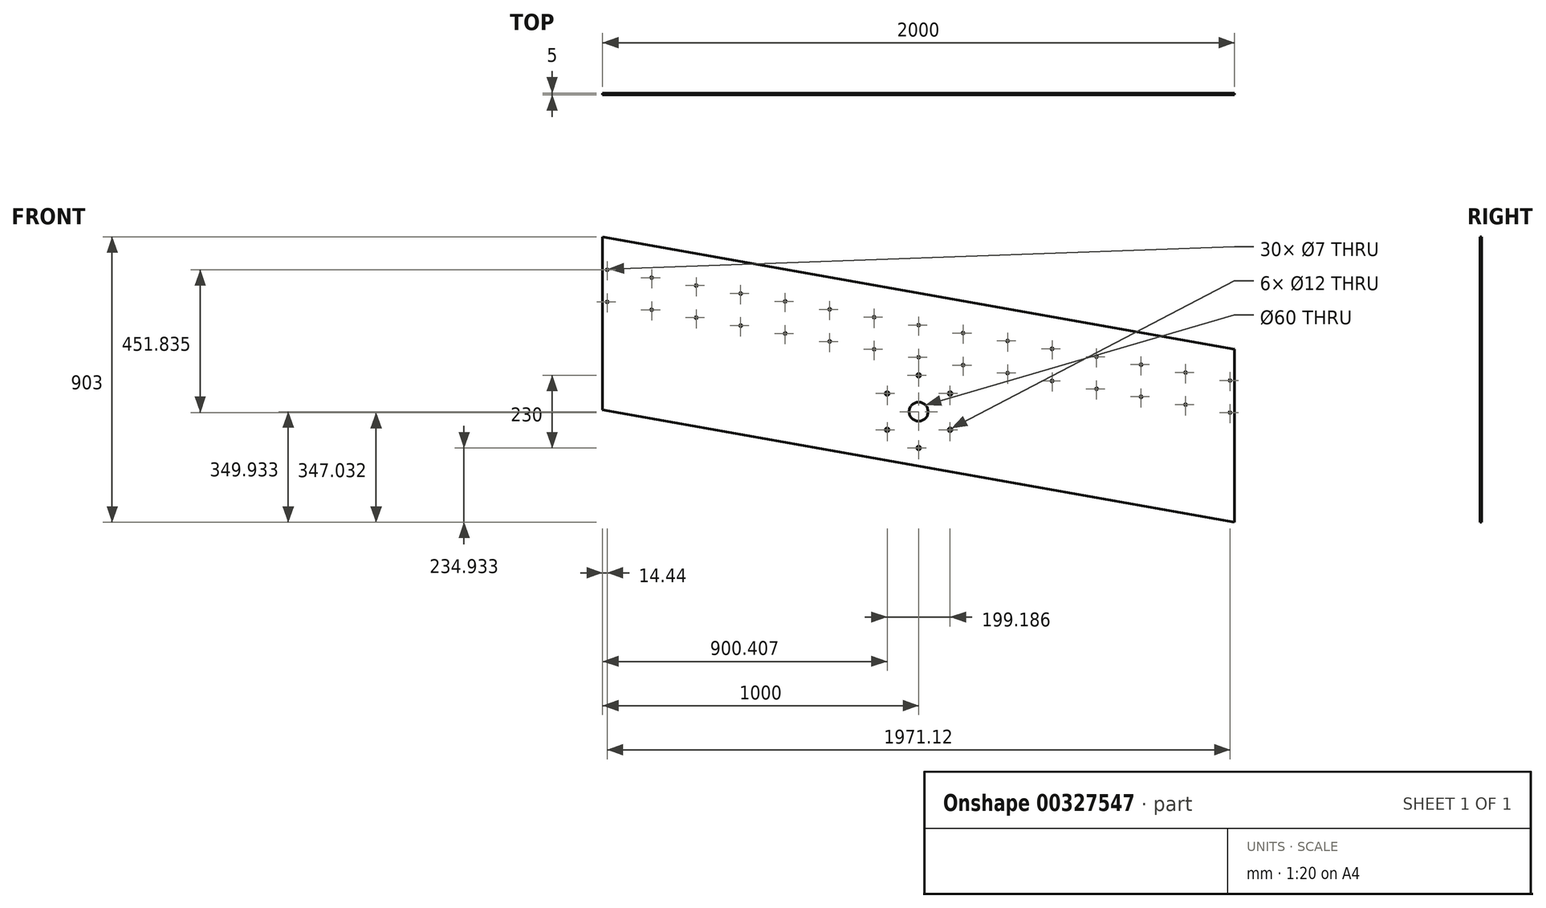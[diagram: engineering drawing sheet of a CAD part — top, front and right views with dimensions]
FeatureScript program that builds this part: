
annotation { "Feature Type Name" : "Feature", "Feature Type Description" : "" }
export const myFeature = defineFeature(function(context is Context, id is Id, definition is map)
    precondition{}
    {
        {
            var Q0;
            Q0=qCreatedBy(makeId("Front.planeOp"),FACE);
            var sketch = newSketch(context, id + "F0", { "sketchPlane" : qUnion([Q0])});
            skLineSegment(sketch, "E0", {"start": v(1435, 0) * mm, "end": v(1435, 547.6) * mm});
            skLineSegment(sketch, "E1", {"start": v(1435, 547.6) * mm, "end": v(-565, 903) * mm});
            skLineSegment(sketch, "E2", {"start": v(-565, 903) * mm, "end": v(-565, 355.4) * mm});
            skLineSegment(sketch, "E3", {"start": v(1435, 344.47) * mm, "end": v(1420.56, 347.03) * mm, "construction": true});
            skCircle(sketch, "E4", {"center": v(-550.56, 798.87) * mm, "radius": 3.5 * mm});
            skCircle(sketch, "E5", {"center": v(-550.56, 697.3) * mm, "radius": 3.5 * mm});
            skLineSegment(sketch, "E6.1.0.0", {"start": v(-409.77, 773.85) * mm, "end": v(-409.77, 672.28) * mm, "construction": true});
            skCircle(sketch, "E6.1.0.1", {"center": v(-409.77, 773.85) * mm, "radius": 3.5 * mm});
            skCircle(sketch, "E6.1.0.2", {"center": v(-409.77, 672.28) * mm, "radius": 3.5 * mm});
            skLineSegment(sketch, "E6.2.0.0", {"start": v(-268.97, 748.83) * mm, "end": v(-268.97, 647.26) * mm, "construction": true});
            skCircle(sketch, "E6.2.0.1", {"center": v(-268.97, 748.83) * mm, "radius": 3.5 * mm});
            skCircle(sketch, "E6.2.0.2", {"center": v(-268.97, 647.26) * mm, "radius": 3.5 * mm});
            skLineSegment(sketch, "E6.3.0.0", {"start": v(-128.18, 723.8) * mm, "end": v(-128.18, 622.24) * mm, "construction": true});
            skCircle(sketch, "E6.3.0.1", {"center": v(-128.18, 723.8) * mm, "radius": 3.5 * mm});
            skCircle(sketch, "E6.3.0.2", {"center": v(-128.18, 622.24) * mm, "radius": 3.5 * mm});
            skLineSegment(sketch, "E6.4.0.0", {"start": v(12.62, 698.8) * mm, "end": v(12.62, 597.22) * mm, "construction": true});
            skCircle(sketch, "E6.4.0.1", {"center": v(12.62, 698.8) * mm, "radius": 3.5 * mm});
            skCircle(sketch, "E6.4.0.2", {"center": v(12.62, 597.22) * mm, "radius": 3.5 * mm});
            skLineSegment(sketch, "E6.5.0.0", {"start": v(153.41, 673.77) * mm, "end": v(153.41, 572.2) * mm, "construction": true});
            skCircle(sketch, "E6.5.0.1", {"center": v(153.41, 673.77) * mm, "radius": 3.5 * mm});
            skCircle(sketch, "E6.5.0.2", {"center": v(153.41, 572.2) * mm, "radius": 3.5 * mm});
            skLineSegment(sketch, "E6.6.0.0", {"start": v(294.2, 648.75) * mm, "end": v(294.2, 547.19) * mm, "construction": true});
            skCircle(sketch, "E6.6.0.1", {"center": v(294.2, 648.75) * mm, "radius": 3.5 * mm});
            skCircle(sketch, "E6.6.0.2", {"center": v(294.2, 547.19) * mm, "radius": 3.5 * mm});
            skLineSegment(sketch, "E6.7.0.0", {"start": v(435, 623.73) * mm, "end": v(435, 522.17) * mm, "construction": true});
            skCircle(sketch, "E6.7.0.1", {"center": v(435, 623.73) * mm, "radius": 3.5 * mm});
            skCircle(sketch, "E6.7.0.2", {"center": v(435, 522.17) * mm, "radius": 3.5 * mm});
            skLineSegment(sketch, "E6.8.0.0", {"start": v(575.8, 598.71) * mm, "end": v(575.8, 497.15) * mm, "construction": true});
            skCircle(sketch, "E6.8.0.1", {"center": v(575.8, 598.71) * mm, "radius": 3.5 * mm});
            skCircle(sketch, "E6.8.0.2", {"center": v(575.8, 497.15) * mm, "radius": 3.5 * mm});
            skLineSegment(sketch, "E6.9.0.0", {"start": v(716.59, 573.7) * mm, "end": v(716.59, 472.13) * mm, "construction": true});
            skCircle(sketch, "E6.9.0.1", {"center": v(716.59, 573.7) * mm, "radius": 3.5 * mm});
            skCircle(sketch, "E6.9.0.2", {"center": v(716.59, 472.13) * mm, "radius": 3.5 * mm});
            skLineSegment(sketch, "E6.10.0.0", {"start": v(857.38, 548.68) * mm, "end": v(857.38, 447.1) * mm, "construction": true});
            skCircle(sketch, "E6.10.0.1", {"center": v(857.38, 548.68) * mm, "radius": 3.5 * mm});
            skCircle(sketch, "E6.10.0.2", {"center": v(857.38, 447.1) * mm, "radius": 3.5 * mm});
            skLineSegment(sketch, "E6.11.0.0", {"start": v(998.18, 523.66) * mm, "end": v(998.18, 422.09) * mm, "construction": true});
            skCircle(sketch, "E6.11.0.1", {"center": v(998.18, 523.66) * mm, "radius": 3.5 * mm});
            skCircle(sketch, "E6.11.0.2", {"center": v(998.18, 422.09) * mm, "radius": 3.5 * mm});
            skLineSegment(sketch, "E6.12.0.0", {"start": v(1138.97, 498.64) * mm, "end": v(1138.97, 397.07) * mm, "construction": true});
            skCircle(sketch, "E6.12.0.1", {"center": v(1138.97, 498.64) * mm, "radius": 3.5 * mm});
            skCircle(sketch, "E6.12.0.2", {"center": v(1138.97, 397.07) * mm, "radius": 3.5 * mm});
            skLineSegment(sketch, "E6.13.0.0", {"start": v(1279.77, 473.62) * mm, "end": v(1279.77, 372.05) * mm, "construction": true});
            skCircle(sketch, "E6.13.0.1", {"center": v(1279.77, 473.62) * mm, "radius": 3.5 * mm});
            skCircle(sketch, "E6.13.0.2", {"center": v(1279.77, 372.05) * mm, "radius": 3.5 * mm});
            skLineSegment(sketch, "E6.14.0.0", {"start": v(1420.56, 448.6) * mm, "end": v(1420.56, 347.03) * mm, "construction": true});
            skCircle(sketch, "E6.14.0.1", {"center": v(1420.56, 448.6) * mm, "radius": 3.5 * mm});
            skCircle(sketch, "E6.14.0.2", {"center": v(1420.56, 347.03) * mm, "radius": 3.5 * mm});
            skLineSegment(sketch, "E6.direction1", {"start": v(-550.56, 697.3) * mm, "end": v(-409.77, 672.28) * mm, "construction": true});
            skLineSegment(sketch, "E7", {"start": v(1420.56, 347.03) * mm, "end": v(-550.56, 697.3) * mm, "construction": true});
            skLineSegment(sketch, "E8", {"start": v(1420.56, 448.6) * mm, "end": v(1435, 446.03) * mm, "construction": true});
            skLineSegment(sketch, "E9", {"start": v(-550.56, 697.3) * mm, "end": v(-565, 699.87) * mm, "construction": true});
            skLineSegment(sketch, "E10", {"start": v(-550.56, 798.87) * mm, "end": v(-550.56, 697.3) * mm, "construction": true});
            skLineSegment(sketch, "E11", {"start": v(-550.56, 798.87) * mm, "end": v(1420.56, 448.6) * mm, "construction": true});
            skLineSegment(sketch, "E12", {"start": v(-550.56, 798.87) * mm, "end": v(-565, 801.43) * mm, "construction": true});
            skLineSegment(sketch, "E13", {"start": v(0, 0) * mm, "end": v(1435, 0) * mm, "construction": true});
            skLineSegment(sketch, "E14", {"start": v(0, 0) * mm, "end": v(0, 255) * mm, "construction": true});
            skLineSegment(sketch, "E15", {"start": v(0, 255) * mm, "end": v(1435, 0) * mm, "construction": true});
            skLineSegment(sketch, "E16", {"start": v(0, 255) * mm, "end": v(-565, 355.4) * mm});
            skLineSegment(sketch, "E17", {"start": v(0, 255) * mm, "end": v(1435, 0) * mm});
            skLineSegment(sketch, "E18", {"start": v(435, 522.17) * mm, "end": v(435, 177.7) * mm, "construction": true});
            skLineSegment(sketch, "E19", {"start": v(435, 349.93) * mm, "end": v(285, 349.93) * mm, "construction": true});
            skPoint(sketch, "E19.endSnap0", {"position": v(435, 349.93) * mm});
            skLineSegment(sketch, "E20", {"start": v(435, 349.93) * mm, "end": v(585, 349.93) * mm, "construction": true});
            skCircle(sketch, "E21", {"center": v(435, 349.93) * mm, "radius": 115 * mm, "construction": true});
            skCircle(sketch, "E22", {"center": v(435, 464.93) * mm, "radius": 6 * mm});
            skCircle(sketch, "E23.1.0", {"center": v(335.4, 407.43) * mm, "radius": 6 * mm});
            skCircle(sketch, "E23.2.0", {"center": v(335.4, 292.43) * mm, "radius": 6 * mm});
            skCircle(sketch, "E23.3.0", {"center": v(435, 234.93) * mm, "radius": 6 * mm});
            skCircle(sketch, "E23.4.0", {"center": v(534.6, 292.43) * mm, "radius": 6 * mm});
            skCircle(sketch, "E23.5.0", {"center": v(534.6, 407.43) * mm, "radius": 6 * mm});
            skCircle(sketch, "E24", {"center": v(435, 349.93) * mm, "radius": 30 * mm});
            skSolve(sketch);
        }
        {
            var Q0;
            Q0=qSketchRegion(id+"F0",true);
            var Q1;
            Q1=makeQuery(id+"F0.imprint","IMPRINT",FACE,{"disambiguationData":[TD([[makeQuery(id+"F0.imprint","IMPRINT",EDGE,{"derivedFrom":sQuery(id+"F0.wireOp",EDGE,"jSg4FRcu-u39U-EJTX-ydAV-j8xegxBfcqbr")}),1.0]])]});
            extrude(context, id + "F1", {"entities" : qUnion([Q0, Q1]), "depth" : 5 * mm, "symmetric" : true});
        }
    });
